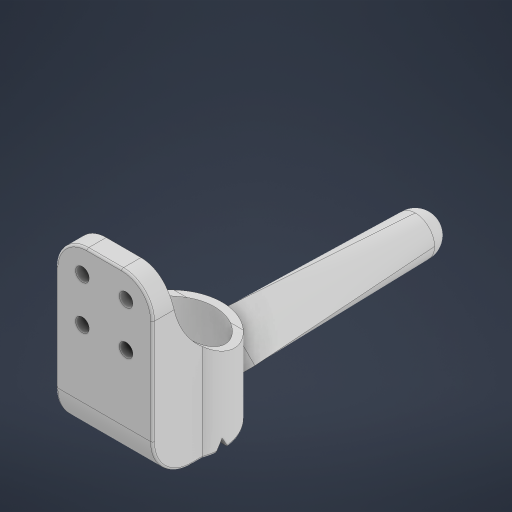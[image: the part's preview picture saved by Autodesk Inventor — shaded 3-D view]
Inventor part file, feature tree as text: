
AUTODESK INVENTOR PART (.ipt)
format: ipt  version: 2023 (Build 270158000, 158)  size: 476,672 bytes
history: native  units: mm
features: sketch x11, extrude x10, fillet x5, plane x4, projected_geometry x2, loft x1, revolve x1, other x1
ambient origin geometry x8: Origin, YZ Plane, XZ Plane, XY Plane, X Axis, Y Axis, Z Axis, Center Point
bodies: Solid1 (feature_tree)
feature tree (35):
  extrude  "Extrusion1"  Depth=2.0mm
  plane  "Work Plane1"
  extrude  "Extrusion2"  Depth=15.5mm
  plane  "Work Plane2"
  extrude  "Extrusion4"  TaperAngle=60.0deg  [1 undecoded]
  sketch  "Sketch7"  dims[d8=3.0mm d9=12.25mm d10=0.0mm]
  extrude  "Extrusion5"  Depth=12.25mm TaperAngle=0.0deg
  extrude  "Extrusion6"  Depth=0.1mm
  fillet  "Fillet1"  Radius=10.25mm
  extrude  "Block Extrusion"  Depth=60.0mm TaperAngle=360.0deg
  extrude  "Extension Extrusion"  Depth=10.0mm TaperAngle=0.0deg
  fillet  "Fillet3"  Radius=5.0mm
  extrude  "Extrusion13"  Depth=25.0mm
  fillet  "Fillet4"  Radius=10.0mm
  extrude  "Extrusion15"  Depth=5.0mm
  plane  "Work Plane6"
  sketch  "Sketch21"  dims[d53=25.0mm d54=0.0mm d55=5.0mm]
  extrude  "Extrusion16"  Depth=16.0mm
  plane  "Work Plane7"
  loft  "Loft2"
  revolve  "Revolution7"  [1 undecoded]
  fillet  "Fillet5"  Radius=10.0mm
  fillet  "Fillet6"  Radius=8.0mm
  sketch  "Sketch1"  dims[d0=22.5mm d1=2.0mm]
  sketch  "Sketch2"  dims[d2=20.0mm d3=0.0mm d4=15.5mm]
  projected_geometry  "Projected Loop1"
  sketch  "Sketch5"  dims[d5=60.0deg d7=60.0deg]
  sketch  "Sketch12"  dims[d14=-20.25mm d16=0.1mm d18=10.25mm d19=0.0mm]
  sketch  "Sketch16"  dims[d20=6.5mm d21=60.0mm d23=360.0deg]
  sketch  "Sketch18"  dims[d25=3.6mm d26=10.0mm d27=0.0mm d28=5.0mm d29=0.0mm]
  sketch  "Sketch20"  dims[d30=3.0mm d39=25.0mm d40=10.0mm d41=0.0mm]
  projected_geometry  "Projected Loop5"
  sketch  "Sketch22"  dims[d56=22.0mm d57=16.0mm]
  other  "Edges1"
  sketch  "Sketch29"  dims[d58=3.5mm d60=12.0mm d61=18.5mm d62=0.0mm d63=10.0mm d64=8.0mm d69=4.0mm d70=10.0mm d71=6.5mm d72=6.5mm d73=6.5mm d74=6.5mm d75=21.5mm d76=0.0mm d77=12.0mm d78=21.5mm d79=0.0mm d80=-50.0mm d82=0.0mm d83=90.0deg d84=0.0mm d85=90.0deg d96=10.0mm d97=360.0deg d98=10.0mm d99=0.5mm d51=0.0mm d52=0.0mm]
note: 2 required parameter values undecoded (feature->parameter linkage not recoverable at this tier; creation-order binding heuristic only, values carry confidence <= 0.55)